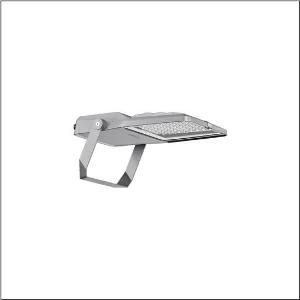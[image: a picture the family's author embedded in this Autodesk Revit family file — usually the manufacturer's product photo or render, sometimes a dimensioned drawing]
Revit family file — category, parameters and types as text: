
# Revit family: floodlight_fl_21_mini___pl52_5xa7775c2d1a_7e4d
name_source: partatom
category: Lighting Fixtures
units: mm (PartAtom-declared; Revit-internal decimal feet)

## family parameters
Cut with Voids When Loaded = No
Host = Face
Light Source = No
Part Type = Normal
Room Calculation Point = No
Round Connector Dimension = Use Diameter
Shared = No

## types (1)
- --- (1 x LED, 12190 lm, 89 W, 3000K)
    Apparent Load = 89 VA
    CIE Flux Codes = 26 60 98 100 100
    Color Rendering = 70
    Color Temperature = 3000K
    Default Elevation = 1800 mm
    Description = Floodlight FL 21 mini, floodlight, primary light control with lens, of PMMA, primary optical cover: protective disc, of toughened safety glass, transparent, light distribution: PL52, light emission: direct distribution, installation type: surface-mounted, LED, High Power LED, rated luminous flux: 12.190lm, luminous efficacy: 137lm/W, light colour: 730, colour temperature: 3000K, control: flexible luminous flux parameterisation, time-dependent luminous flux control, constant luminous flux control, overheat protection, presetting dimming logarithmic, with terminal, 6-pole, mains connection: 220..240V, AC, 50/60Hz, start of lifetime: 89W, end of service life: 94W, reduction: 43W, luminaire housing, of diecast aluminium, powder-coated, Siteco® metallic grey (DB 702S), corrosivity category C5 mid according to DIN EN ISO 12944, sealing non-destructively replaceable, mounting bracket, of steel, galvanised, powder-coated, Siteco® metallic grey (DB 702S), Smart Interface above, protection rating (complete): IP66, insulation class (complete): insulation class II (safety insulation), certification: CE, ENEC, VDE, protection symbol: D, impact resistance: IK08, permissible operating ambient temperature: -40..+40°C, permissible operating ambient temperature for outdoor applications: -40..+50°C, standard: DIN EN 12944, LABS conformity tested according to VDMA 24364:2018-05, packaging unit: 1 piece

Light Distribution: PL52
    Height = 70 mm
    Lamp = 1 x LED
    Lamp Light Flux = 12190 lm
    Lamp Power = 89 W
    Lamp count = 1
    Length = 485 mm
    Luminous efficacy = 137 lm/W
    Manufacturer = Siteco
    ModVariant = No
    Model = 5XA7775C2D1A
    Number of Poles = 1
    OnlyDefault = Yes
    Power Factor = 1
    Product Name = Floodlight FL 21 mini | PL52
    Product group = floodlight | pylon annexe
    ProductGroupID = 6200
    Protection Class = Protection class II
    Protection Degree = IP 66
    RLX_Detail_Level = 1
    RLX_Emergency_Light_Flux = 0 lm
    RLX_Emergency_Type = 0
    RLX_Emergency_Type_DB = No
    RlxData = <blob elided: 96001 chars, md5=3d47230d>
    Socket = socket
    Standby Power = 0 W
    System Light Flux = 12190 lm
    System Power = 89 W
    Type Comments = factory setting: luminous flux: 100 % | dim-lin: 254 | 456 mA
    Type Image = l_1006845.jpg
    URL = http://relux.com
    VarID = @adj_095653
    Voltage = 0 V
    Weight = 0.00 kg
    Width = 337 mm

## geometry (parser evidence)
native form markers: Blend x4, Sweep x12
no freeform markers — native parametric forms only
